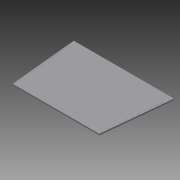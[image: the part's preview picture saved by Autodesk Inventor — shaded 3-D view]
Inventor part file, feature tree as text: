
AUTODESK INVENTOR PART (.ipt)
format: ipt  version: 2015 (Build 190159000, 159)  size: 80,896 bytes
history: native  units: in
note: dims shown in document units (in); Inventor stores cm internally (conversion verified against a paired STEP export)
features: extrude x1, sketch x1, reference x1
ambient origin geometry x8: Origin, YZ Plane, XZ Plane, XY Plane, X Axis, Y Axis, Z Axis, Center Point
bodies: Solid1 (feature_tree)
feature tree (3):
  extrude  "Extrusion1"  Depth=0.25in TaperAngle=0.0deg
  sketch  "Sketch1"  dims[d0=0.25in d1=0.25in d2=0.0in]
  reference  "Reference1"
